# Revit family: WashbasinUnit-Vitra-EqualSeries-64085-64086-64088-64094-64097
name_source: partatom
category: Furniture Systems
revit_build: Autodesk Revit 2017 (Build: 20160225_1515(x64)
units: mm (PartAtom-declared; Revit-internal decimal feet)

## family parameters
Cut with Voids When Loaded = No
Host = Face
OmniClass Number = 23.40.00.00
OmniClass Title = Equipment and Furnishings
Part Type = Normal
Room Calculation Point = No
Round Connector Dimension = Use Diameter
Shared = Yes

## types (5) — shared parameters
BIMobject category = Bathroom compound units
Construction Type = Face Mounted
Default Elevation = 660 mm
Depth(mm) = 515 mm  [stored 1.68963 ft]
Design country = Turkey
Height(mm) = 183 mm
IFC Classification = Furniture
Manufacturer = Vitra
Manufacturer name = Vitra
Masterformat 2014 Code = 13 42 13
Masterformat 2014 Description = Bathroom Unit Modules
NBS Referans Code = 35-75-08
NBS Referans Description = Bathroom Cabinets
Nominal height = 0.000
Nominal width = 0.000
OmniClass Code = 23-31 25 13
OmniClass Description = Bathroom Cabinets
Product certification = https://vitraglobal.com
Product data url = https://www.vitraglobal.com
Product family = Equal
Product group = Washbasin Unit
Technical description = https://www.vitra.com.tr
UNSPSC Code = 301815
UNSPSC Description = Bathroom Cabinets
URL = https://vitraglobal.com
Uniclass 1.4 Code = L8241
Uniclass 1.4 Description = Bathroom Cabinets
Uniclass 2.0 Code = PR-35-75-08
Uniclass 2.0 Description = Bathroom Cabinets
Uniclass 2015 Code = Pr_40_20_93
Uniclass 2015 Name = Wash basins, sinks and troughs
Uniformat II Code = E20
Uniformat II Description = FURNISHINGS
Warranty Period (Year) = 2
Youtube = https://www.youtube.com

## per-type parameters (varying)
| type | Article No. (default) | Description | Model | Primary Material | Product SKU | Towel Holder | Weight Net (kg) | Width(mm) |
| WashbasinUnit-WithTowelHolder-Vitra-EqualSeries-100cm_64088 | 64088 | Equal Washbasin Unit, 100 cm, with Asymmetric Washbasin, with Towel Holder | 64088 | Vitra-Matte Black | 64088 | Yes | 36,600 | 1026 mm |
| WashbasinUnit-WithDoubleWashbasin-WithTowelHolder-Vitra-EqualSeries-130cm_64097 | 64097 | Equal Washbasin Unit, 130 cm, with Double Washbasin, with Towel Holder | 64097 | Vitra-Matte Black | 64097 | Yes | 38,000 | 1325 mm  [stored 4.34711 ft] |
| WashbasinUnit-WithAsymmetricWashbasin-Vitra-EqualSeries-100cm_64085 | 64085 | Equal Washbasin Unit, 100 cm, with Asymmetric Washbasin, | 64085 | Vitra-Matte Black | 64085 | No | 37,500 | 1026 mm |
| WashbasinUnit-WithAsymmetricWashbasin-Vitra-EqualSeries-100cm_64086 | 64086 | Equal Washbasin Unit, 100 cm, with Asymmetric Washbasin, | 64086 | Vitra-Elm | 64086 | No | 37,500 | 1026 mm |
| WashbasinUnit-WithDoubleWashbasin-Vitra-EqualSeries-130cm_64094 | 64094 | Equal Washbasin Unit, 130 cm, with Double Washbasin | 64094 | Vitra-Matte Black | 64094 | No | 33,800 | 1325 mm  [stored 4.34711 ft] |

note: [stored X ft] marks values corroborated as IEEE doubles in the binary element streams (Revit-internal decimal feet)

## geometry (parser evidence)
native form markers: Sweep x2
no freeform markers — native parametric forms only
